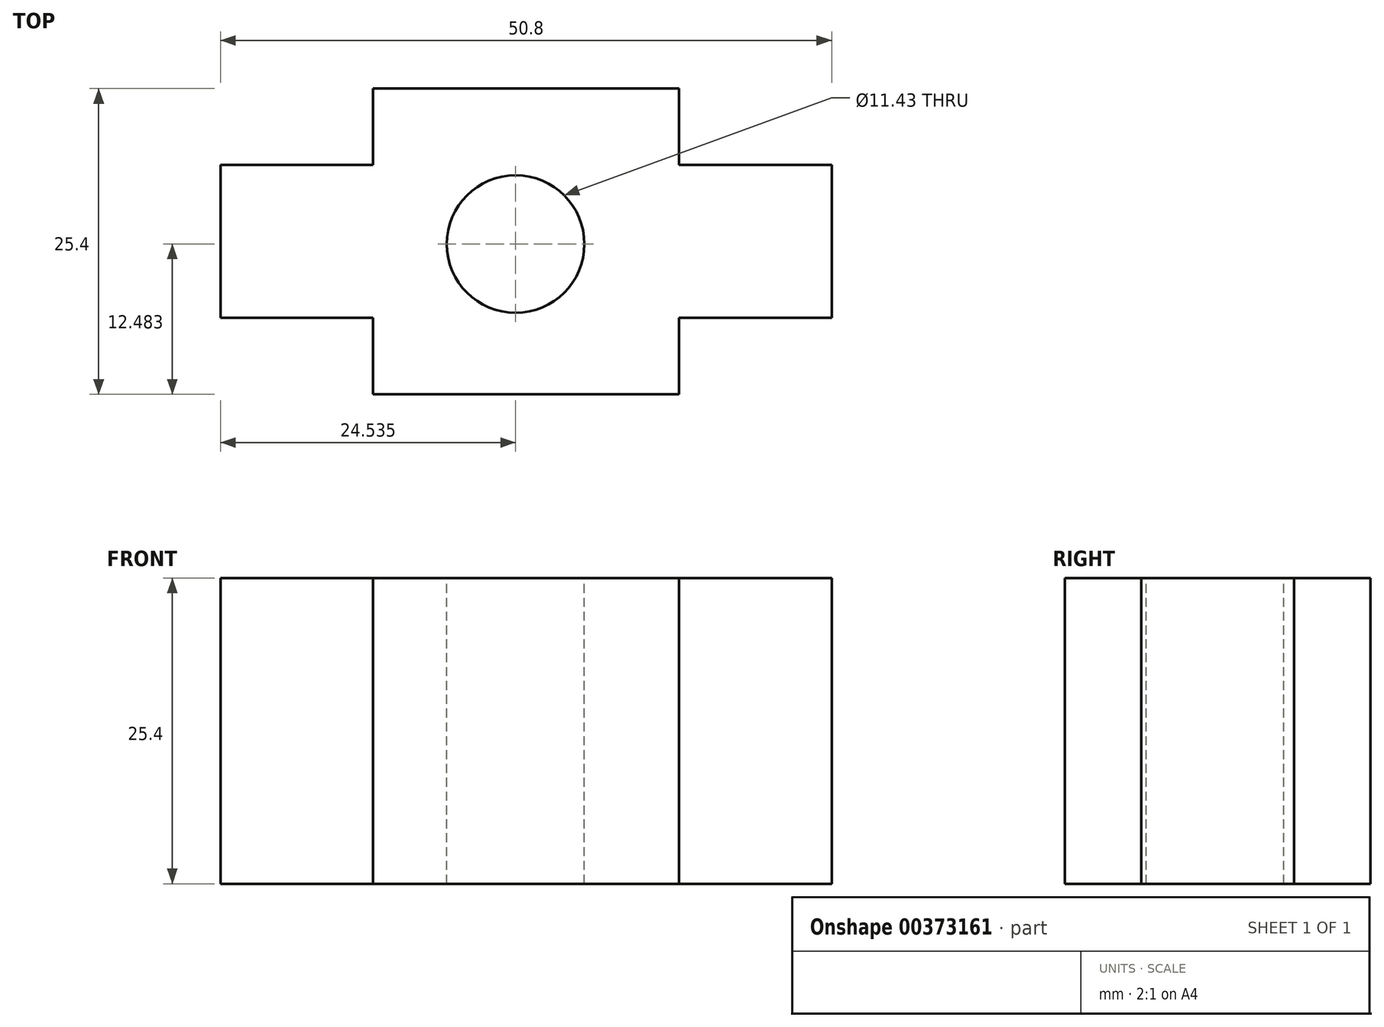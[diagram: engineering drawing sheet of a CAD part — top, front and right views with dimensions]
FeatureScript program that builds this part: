
annotation { "Feature Type Name" : "Feature", "Feature Type Description" : "" }
export const myFeature = defineFeature(function(context is Context, id is Id, definition is map)
    precondition{}
    {
        {
            var Q0;
            Q0=qCreatedBy(makeId("Front.planeOp"),FACE);
            var sketch = newSketch(context, id + "F0", { "sketchPlane" : qUnion([Q0])});
            skLineSegment(sketch, "E0", {"start": v(0, 0) * mm, "end": v(0, 25.4) * mm});
            skLineSegment(sketch, "E1", {"start": v(0, 25.4) * mm, "end": v(50.8, 25.4) * mm});
            skLineSegment(sketch, "E2", {"start": v(50.8, 25.4) * mm, "end": v(50.8, 0) * mm});
            skLineSegment(sketch, "E3", {"start": v(50.8, 0) * mm, "end": v(0, 0) * mm});
            skSolve(sketch);
        }
        {
            var Q0;
            Q0 = qSketchRegion(id + "F0", true);
            extrude(context, id + "F1", {"entities" : qUnion([Q0]), "oppositeDirection" : true, "depth" : 25.4 * mm});
        }
        {
            var Q0;
            Q0=makeQuery(id+"F1.opExtrude","SWEPT_FACE",FACE,{"disambiguationData":[OSD([sQuery(id+"F0.wireOp",EDGE,"E1")])]});
            var sketch = newSketch(context, id + "F2", { "sketchPlane" : qUnion([Q0])});
            skCircle(sketch, "E4", {"center": v(24.53, 12.48) * mm, "radius": 5.72 * mm});
            skLineSegment(sketch, "E5", {"start": v(0, 25.4) * mm, "end": v(0, 19.05) * mm});
            skLineSegment(sketch, "E6", {"start": v(0, 19.05) * mm, "end": v(12.7, 19.05) * mm});
            skLineSegment(sketch, "E7", {"start": v(12.7, 19.05) * mm, "end": v(12.7, 25.4) * mm});
            skLineSegment(sketch, "E8", {"start": v(12.7, 25.4) * mm, "end": v(0, 25.4) * mm});
            skLineSegment(sketch, "E9", {"start": v(50.8, 25.4) * mm, "end": v(50.8, 19.05) * mm});
            skLineSegment(sketch, "E10", {"start": v(50.8, 19.05) * mm, "end": v(38.1, 19.05) * mm});
            skLineSegment(sketch, "E11", {"start": v(38.1, 19.05) * mm, "end": v(38.1, 25.4) * mm});
            skLineSegment(sketch, "E12", {"start": v(38.1, 25.4) * mm, "end": v(50.8, 25.4) * mm});
            skLineSegment(sketch, "E13", {"start": v(0, 0) * mm, "end": v(0, 6.35) * mm});
            skLineSegment(sketch, "E14", {"start": v(0, 6.35) * mm, "end": v(12.7, 6.35) * mm});
            skLineSegment(sketch, "E15", {"start": v(12.7, 6.35) * mm, "end": v(12.7, 0) * mm});
            skLineSegment(sketch, "E16", {"start": v(12.7, 0) * mm, "end": v(0, 0) * mm});
            skLineSegment(sketch, "E17", {"start": v(50.8, 0) * mm, "end": v(50.8, 6.35) * mm});
            skLineSegment(sketch, "E18", {"start": v(50.8, 6.35) * mm, "end": v(38.1, 6.35) * mm});
            skLineSegment(sketch, "E19", {"start": v(38.1, 6.35) * mm, "end": v(38.1, 0) * mm});
            skLineSegment(sketch, "E20", {"start": v(38.1, 0) * mm, "end": v(50.8, 0) * mm});
            skSolve(sketch);
        }
        {
            var Q0;
            Q0 = qSketchRegion(id + "F2", true);
            extrude(context, id + "F3", {"entities" : qUnion([Q0]), "operationType" : NewBodyOperationType.REMOVE, "oppositeDirection" : true, "depth" : 25.4 * mm});
        }
    });
